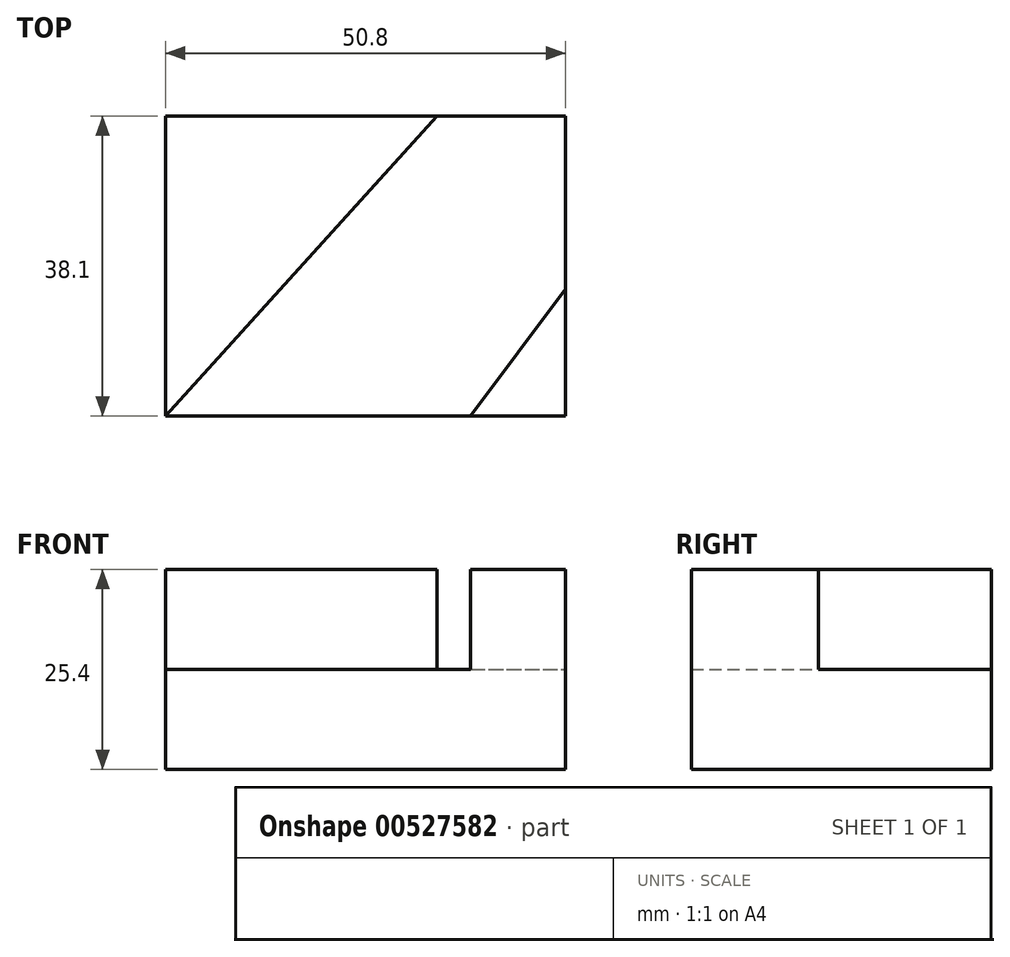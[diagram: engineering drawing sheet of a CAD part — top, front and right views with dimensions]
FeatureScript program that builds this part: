
annotation { "Feature Type Name" : "Feature", "Feature Type Description" : "" }
export const myFeature = defineFeature(function(context is Context, id is Id, definition is map)
    precondition{}
    {
        {
            var Q0;
            Q0=qCreatedBy(makeId("Front.planeOp"),FACE);
            var sketch = newSketch(context, id + "F0", { "sketchPlane" : qUnion([Q0])});
            skLineSegment(sketch, "E0", {"start": v(0, 0) * mm, "end": v(50.8, 0) * mm});
            skLineSegment(sketch, "E1", {"start": v(50.8, 0) * mm, "end": v(50.8, 25.4) * mm});
            skLineSegment(sketch, "E2", {"start": v(50.8, 25.4) * mm, "end": v(0, 25.4) * mm});
            skLineSegment(sketch, "E3", {"start": v(0, 25.4) * mm, "end": v(0, 0) * mm});
            skSolve(sketch);
        }
        {
            var Q0;
            Q0=makeQuery(id+"F0.imprint","IMPRINT",FACE,{"disambiguationData":[TD([[makeQuery(id+"F0.imprint","IMPRINT",EDGE,{"derivedFrom":sQuery(id+"F0.wireOp",EDGE,"E0")}),1.0]])]});
            extrude(context, id + "F1", {"entities" : qUnion([Q0]), "depth" : 38.1 * mm, "offsetDistance" : 25.4 * mm});
        }
        {
            var Q0;
            Q0=makeQuery(id+"F1.opExtrude","SWEPT_FACE",FACE,{"disambiguationData":[OSD([sQuery(id+"F0.wireOp",EDGE,"E2")])]});
            var sketch = newSketch(context, id + "F2", { "sketchPlane" : qUnion([Q0])});
            skLineSegment(sketch, "E4", {"start": v(38.73, -38.1) * mm, "end": v(50.8, -21.99) * mm});
            skSolve(sketch);
        }
        {
            var Q0;
            {var subQ0=sQuery(id+"F2.wireOp",EDGE,"E4");Q0=makeQuery(id+"F2.imprint","IMPRINT",FACE,{"disambiguationData":[TD([[makeQuery(id+"F2.imprint","IMPRINT",EDGE,{"derivedFrom":subQ0}),-1.0]])]});}
            var sketch = newSketch(context, id + "F3", { "sketchPlane" : qUnion([Q0])});
            skLineSegment(sketch, "E5.0", {"start": v(0, -38.1) * mm, "end": v(34.5, 0) * mm});
            skLineSegment(sketch, "E6.0", {"start": v(38.73, -38.1) * mm, "end": v(50.8, -21.99) * mm});
            skLineSegment(sketch, "E7", {"start": v(0, -38.1) * mm, "end": v(38.73, -38.1) * mm});
            skLineSegment(sketch, "E8", {"start": v(34.5, 0) * mm, "end": v(50.8, 0) * mm});
            skLineSegment(sketch, "E9", {"start": v(50.8, 0) * mm, "end": v(50.8, -21.99) * mm});
            skSolve(sketch);
        }
        {
            var Q0;
            Q0=makeQuery(id+"F3.imprint","IMPRINT",FACE,{"disambiguationData":[TD([[makeQuery(id+"F3.imprint","IMPRINT",EDGE,{"derivedFrom":sQuery(id+"F3.wireOp",EDGE,"E5.0")}),-1.0]])]});
            extrude(context, id + "F4", {"entities" : qUnion([Q0]), "operationType" : NewBodyOperationType.REMOVE, "oppositeDirection" : true, "depth" : 12.7 * mm, "offsetDistance" : 25.4 * mm});
        }
    });
